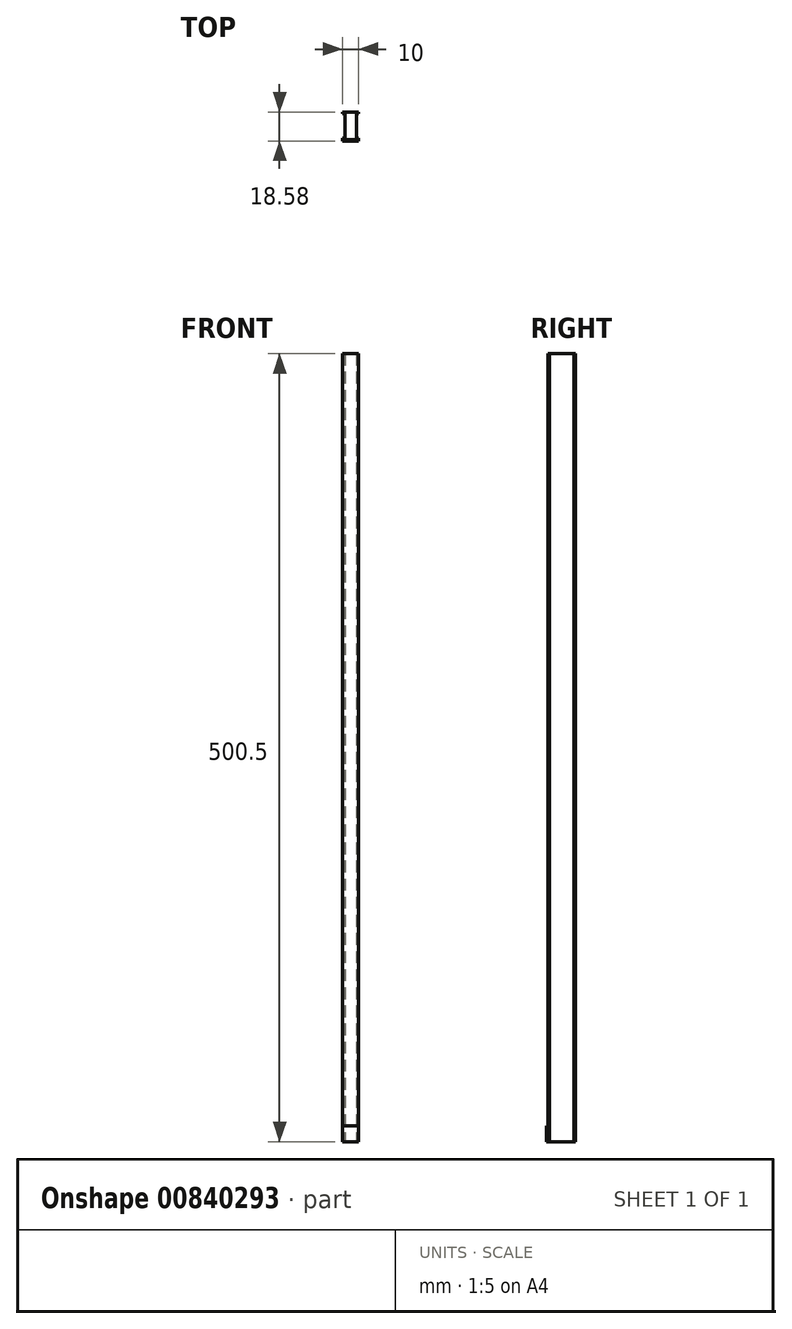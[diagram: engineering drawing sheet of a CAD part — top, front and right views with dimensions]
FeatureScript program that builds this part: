
annotation { "Feature Type Name" : "Feature", "Feature Type Description" : "" }
export const myFeature = defineFeature(function(context is Context, id is Id, definition is map)
    precondition{}
    {
        {
            var Q0;
            Q0=qCreatedBy(makeId("Top.planeOp"),FACE);
            var sketch = newSketch(context, id + "F0", { "sketchPlane" : qUnion([Q0])});
            skLineSegment(sketch, "E0", {"start": v(-5, 15.44) * mm, "end": v(5, 15.44) * mm});
            skLineSegment(sketch, "E1", {"start": v(5, 15.44) * mm, "end": v(5, 14.44) * mm});
            skLineSegment(sketch, "E2", {"start": v(-5, 15.44) * mm, "end": v(-5, 14.44) * mm});
            skLineSegment(sketch, "E3", {"start": v(-5, 14.44) * mm, "end": v(-3.67, 14.44) * mm});
            skLineSegment(sketch, "E4", {"start": v(5, 14.44) * mm, "end": v(3.67, 14.44) * mm});
            skLineSegment(sketch, "E5", {"start": v(-3.67, 14.44) * mm, "end": v(-3.67, -1.14) * mm});
            skLineSegment(sketch, "E6", {"start": v(3.67, 14.44) * mm, "end": v(3.67, -1.14) * mm});
            skLineSegment(sketch, "E7", {"start": v(-3.67, -1.14) * mm, "end": v(-5, -1.14) * mm});
            skLineSegment(sketch, "E8", {"start": v(3.67, -1.14) * mm, "end": v(5, -1.14) * mm});
            skLineSegment(sketch, "E9", {"start": v(-5, -1.14) * mm, "end": v(-5, -2.14) * mm});
            skLineSegment(sketch, "E10", {"start": v(5, -1.14) * mm, "end": v(5, -2.14) * mm});
            skLineSegment(sketch, "E11", {"start": v(-5, -2.14) * mm, "end": v(5, -2.14) * mm});
            skSolve(sketch);
        }
        {
            var Q0;
            Q0=makeQuery(id+"F0.imprint","IMPRINT",FACE,{"disambiguationData":[TD([[makeQuery(id+"F0.imprint","IMPRINT",EDGE,{"derivedFrom":sQuery(id+"F0.wireOp",EDGE,"E0")}),-1.0]])]});
            extrude(context, id + "F1", {"entities" : qUnion([Q0]), "depth" : 500.5 * mm, "offsetDistance" : 25 * mm});
        }
        {
            var Q0;
            Q0=makeQuery(id+"F1.opExtrude","SWEPT_FACE",FACE,{"disambiguationData":[OSD([sQuery(id+"F0.wireOp",EDGE,"E11")])]});
            var sketch = newSketch(context, id + "F2", { "sketchPlane" : qUnion([Q0])});
            skLineSegment(sketch, "E12", {"start": v(-5, 0) * mm, "end": v(5, 0) * mm});
            skLineSegment(sketch, "E13", {"start": v(5, 0) * mm, "end": v(5, 10) * mm});
            skLineSegment(sketch, "E14", {"start": v(5, 10) * mm, "end": v(-5, 10) * mm});
            skLineSegment(sketch, "E15", {"start": v(-5, 10) * mm, "end": v(-5, 0) * mm});
            skSolve(sketch);
        }
        {
            var Q0;
            Q0=makeQuery(id+"F2.imprint","IMPRINT",FACE,{"disambiguationData":[TD([[makeQuery(id+"F2.imprint","IMPRINT",EDGE,{"derivedFrom":sQuery(id+"F2.wireOp",EDGE,"E12")}),1.0]])]});
            extrude(context, id + "F3", {"entities" : qUnion([Q0]), "operationType" : NewBodyOperationType.ADD, "depth" : 1 * mm, "offsetDistance" : 25 * mm});
        }
    });
